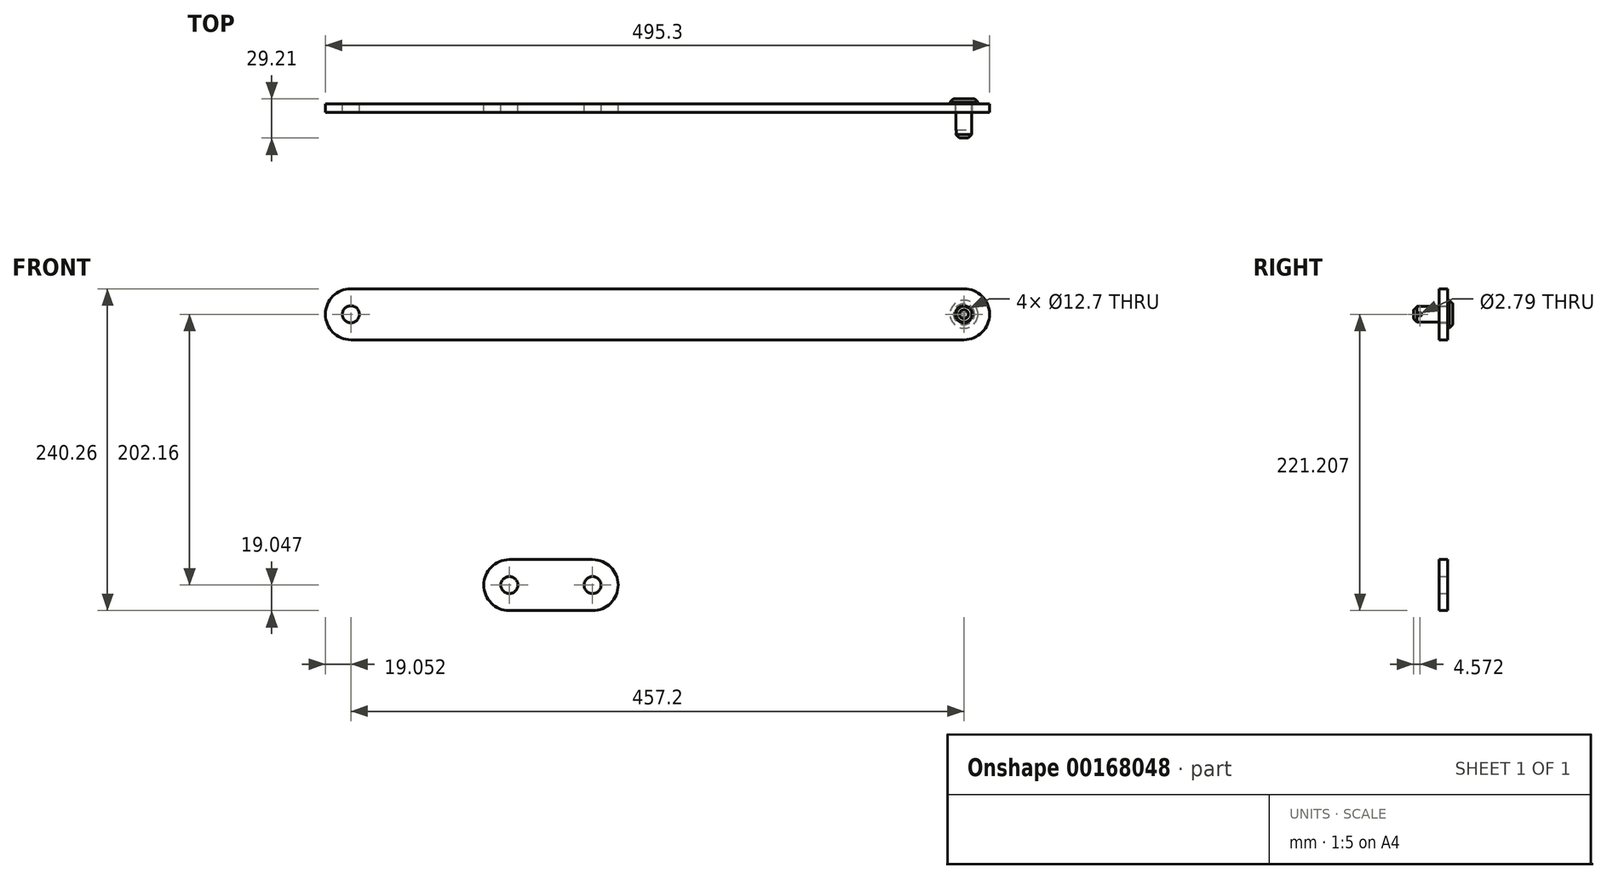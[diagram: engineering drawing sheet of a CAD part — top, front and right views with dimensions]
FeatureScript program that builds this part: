
annotation { "Feature Type Name" : "Feature", "Feature Type Description" : "" }
export const myFeature = defineFeature(function(context is Context, id is Id, definition is map)
    precondition{}
    {
        {
            var Q0;
            Q0=qCreatedBy(makeId("Front.planeOp"),FACE);
            var sketch = newSketch(context, id + "F0", { "sketchPlane" : qUnion([Q0])});
            skLineSegment(sketch, "E0", {"start": v(-17.99, 73.73) * mm, "end": v(439.21, 73.73) * mm});
            skLineSegment(sketch, "E1", {"start": v(-17.99, 35.63) * mm, "end": v(439.21, 35.63) * mm});
            skArc(sketch, "E2", {"start": v(-17.99, 73.73) * mm, "mid": v(-37.04, 54.68) * mm, "end": v(-17.99, 35.63) * mm});
            skArc(sketch, "E3", {"start": v(439.21, 73.73) * mm, "mid": v(458.26, 54.68) * mm, "end": v(439.21, 35.63) * mm});
            skCircle(sketch, "E4", {"center": v(-17.99, 54.68) * mm, "radius": 6.35 * mm});
            skCircle(sketch, "E5", {"center": v(439.21, 54.68) * mm, "radius": 6.35 * mm});
            skSolve(sketch);
        }
        {
            var Q0;
            Q0=makeQuery(id+"F0.imprint","IMPRINT",FACE,{"disambiguationData":[TD([[makeQuery(id+"F0.imprint","IMPRINT",EDGE,{"derivedFrom":sQuery(id+"F0.wireOp",EDGE,"E0")}),-1.0]])]});
            extrude(context, id + "F1", {"entities" : qUnion([Q0]), "depth" : 6.35 * mm});
        }
        {
            var Q0;
            Q0=makeQuery(id+"F1.opExtrude","CAP_FACE",FACE,{"disambiguationData":[OSD([sQuery(id+"F0.wireOp",EDGE,"E0"),sQuery(id+"F0.wireOp",EDGE,"E1"),sQuery(id+"F0.wireOp",EDGE,"E2"),sQuery(id+"F0.wireOp",EDGE,"E3"),sQuery(id+"F0.wireOp",EDGE,"E4"),sQuery(id+"F0.wireOp",EDGE,"E5")])],"isStart":true});
            var sketch = newSketch(context, id + "F2", { "sketchPlane" : qUnion([Q0])});
            skCircle(sketch, "E6.0", {"center": v(-439.21, 54.68) * mm, "radius": 6.35 * mm});
            skCircle(sketch, "E7", {"center": v(-439.21, 54.68) * mm, "radius": 5.89 * mm});
            skCircle(sketch, "E8", {"center": v(-439.21, 54.68) * mm, "radius": 10.44 * mm});
            skSolve(sketch);
        }
        {
            var Q0;
            Q0=makeQuery(id+"F2.imprint","IMPRINT",FACE,{"disambiguationData":[TD([[makeQuery(id+"F2.imprint","IMPRINT",EDGE,{"derivedFrom":sQuery(id+"F2.wireOp",EDGE,"E7")}),1.0]])]});
            extrude(context, id + "F3", {"entities" : qUnion([Q0]), "oppositeDirection" : true, "depth" : 25.4 * mm});
        }
        {
            var Q0;
            Q0=makeQuery(id+"F2.imprint","IMPRINT",FACE,{"disambiguationData":[TD([[makeQuery(id+"F2.imprint","IMPRINT",EDGE,{"derivedFrom":sQuery(id+"F2.wireOp",EDGE,"E7")}),1.0]])]});
            var Q1;
            Q1=makeQuery(id+"F2.imprint","IMPRINT",FACE,{"disambiguationData":[TD([[makeQuery(id+"F2.imprint","IMPRINT",EDGE,{"derivedFrom":sQuery(id+"F2.wireOp",EDGE,"E6.0")}),-1.0]])]});
            var Q2;
            Q2=makeQuery(id+"F2.imprint","IMPRINT",FACE,{"disambiguationData":[TD([[makeQuery(id+"F2.imprint","IMPRINT",EDGE,{"derivedFrom":sQuery(id+"F2.wireOp",EDGE,"E6.0")}),1.0]])]});
            extrude(context, id + "F4", {"entities" : qUnion([Q0, Q1, Q2]), "depth" : 3.8 * mm});
        }
        {
            var Q0;
            Q0=makeQuery(id+"F4.opExtrude","CAP_EDGE",EDGE,{"disambiguationData":[OSD([sQuery(id+"F2.wireOp",EDGE,"E8")])],"isStart":false});
            var Q1;
            Q1=makeQuery(id+"F3.opExtrude","CAP_EDGE",EDGE,{"disambiguationData":[OSD([sQuery(id+"F2.wireOp",EDGE,"E7")])],"isStart":false});
            chamfer(context, id + "F5", {"entities" : qUnion([Q0, Q1]), "width" : 2.54 * mm, "tangentPropagation" : true});
        }
        {
            var Q0;
            Q0=makeQuery(id+"F4.opExtrude","CAP_FACE",FACE,{"disambiguationData":[OSD([sQuery(id+"F2.wireOp",EDGE,"E8")])],"isStart":false});
            var sketch = newSketch(context, id + "F6", { "sketchPlane" : qUnion([Q0])});
            skCircle(sketch, "E9.0", {"center": v(-439.21, 54.68) * mm, "radius": 7.9 * mm});
            skLineSegment(sketch, "E10", {"start": v(-54.11, 54.68) * mm, "end": v(-439.21, 54.68) * mm, "construction": true});
            skCircle(sketch, "E11.0", {"center": v(-439.21, 54.68) * mm, "radius": 5.89 * mm});
            skPoint(sketch, "E12", {"position": v(-445.1, 54.68) * mm});
            skSolve(sketch);
        }
        {
            var Q0;
            Q0=sQuery(id+"F6.wireOp",VERTEX,"E12");
            var Q1;
            Q1=sQuery(id+"F6.wireOp",EDGE,"E10");
            cPlane(context, id + "F7", {"entities" : qUnion([Q0, Q1]), "cplaneType" : CPlaneType.LINE_POINT, "offset" : 25.4 * mm, "width" : 152.4 * mm, "height" : 152.4 * mm});
        }
        {
            var Q0;
            Q0=qCreatedBy(id+"F7.planeOp",FACE);
            var sketch = newSketch(context, id + "F8", { "sketchPlane" : qUnion([Q0])});
            skPoint(sketch, "E13.0", {"position": v(3.81, 54.68) * mm});
            skLineSegment(sketch, "E14", {"start": v(3.81, 54.68) * mm, "end": v(-26.32, 54.68) * mm, "construction": true});
            skPoint(sketch, "E15", {"position": v(-20.83, 54.68) * mm});
            skCircle(sketch, "E16", {"center": v(-20.83, 54.68) * mm, "radius": 1.4 * mm});
            skSolve(sketch);
        }
        {
            var Q0;
            Q0=makeQuery(id+"F8.imprint","IMPRINT",FACE,{"disambiguationData":[TD([[makeQuery(id+"F8.imprint","IMPRINT",EDGE,{"derivedFrom":sQuery(id+"F8.wireOp",EDGE,"E16")}),1.0]])]});
            extrude(context, id + "F9", {"entities" : qUnion([Q0]), "operationType" : NewBodyOperationType.REMOVE, "endBound" : BoundingType.THROUGH_ALL, "oppositeDirection" : true, "depth" : 25.4 * mm});
        }
        {
            var Q0;
            Q0=qCreatedBy(makeId("Front.planeOp"),FACE);
            var sketch = newSketch(context, id + "F10", { "sketchPlane" : qUnion([Q0])});
            skLineSegment(sketch, "E17", {"start": v(100.17, -128.43) * mm, "end": v(162.22, -128.43) * mm});
            skArc(sketch, "E18", {"start": v(162.22, -128.43) * mm, "mid": v(181.27, -147.48) * mm, "end": v(162.22, -166.53) * mm});
            skLineSegment(sketch, "E19", {"start": v(162.22, -166.53) * mm, "end": v(100.17, -166.53) * mm});
            skArc(sketch, "E20", {"start": v(100.17, -166.53) * mm, "mid": v(81.12, -147.48) * mm, "end": v(100.17, -128.43) * mm});
            skCircle(sketch, "E21", {"center": v(100.17, -147.48) * mm, "radius": 6.35 * mm});
            skCircle(sketch, "E22", {"center": v(162.22, -147.48) * mm, "radius": 6.35 * mm});
            skSolve(sketch);
        }
        {
            var Q0;
            Q0=makeQuery(id+"F10.imprint","IMPRINT",FACE,{"disambiguationData":[TD([[makeQuery(id+"F10.imprint","IMPRINT",EDGE,{"derivedFrom":sQuery(id+"F10.wireOp",EDGE,"E17")}),-1.0]])]});
            extrude(context, id + "F11", {"entities" : qUnion([Q0]), "depth" : 6.35 * mm});
        }
    });
